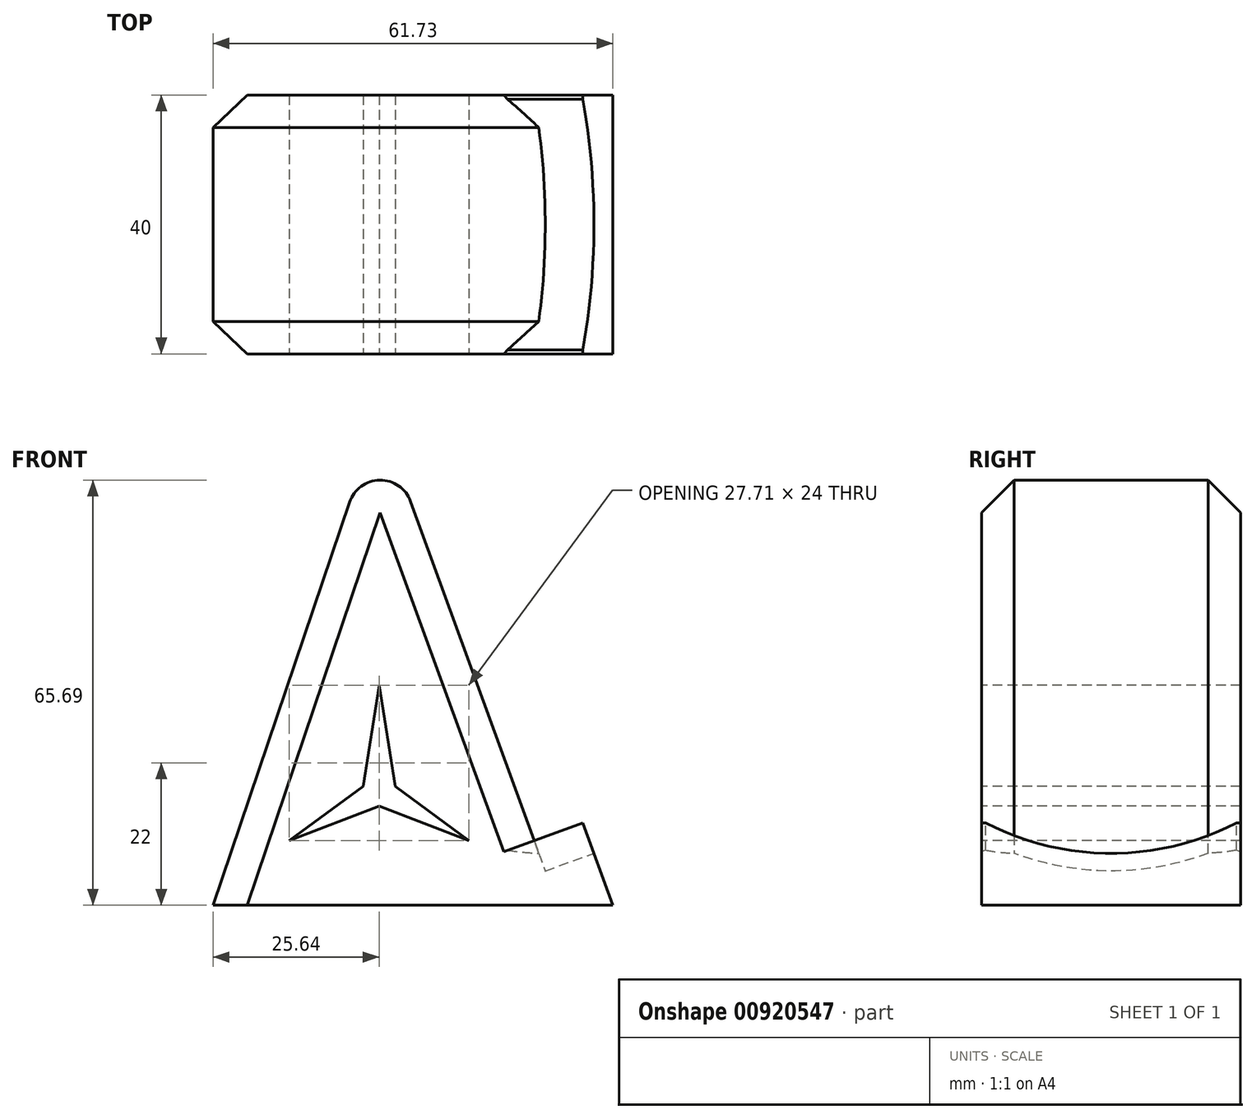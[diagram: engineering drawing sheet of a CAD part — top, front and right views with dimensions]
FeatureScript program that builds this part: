
annotation { "Feature Type Name" : "Feature", "Feature Type Description" : "" }
export const myFeature = defineFeature(function(context is Context, id is Id, definition is map)
    precondition{}
    {
        {
            var Q0;
            Q0=qCreatedBy(makeId("Front.planeOp"),FACE);
            var sketch = newSketch(context, id + "F0", { "sketchPlane" : qUnion([Q0])});
            skLineSegment(sketch, "E0", {"start": v(0, 0) * mm, "end": v(36.1, 0) * mm});
            skLineSegment(sketch, "E1", {"start": v(36.1, 0) * mm, "end": v(31.46, 12.74) * mm});
            skLineSegment(sketch, "E2", {"start": v(31.46, 12.74) * mm, "end": v(23.94, 10) * mm});
            skLineSegment(sketch, "E3", {"start": v(23.94, 10) * mm, "end": v(0, 75.78) * mm});
            skLineSegment(sketch, "E4", {"start": v(0, 75.78) * mm, "end": v(0, 0) * mm, "construction": true});
            skLineSegment(sketch, "E5", {"start": v(0, 75.78) * mm, "end": v(-25.64, 0) * mm});
            skLineSegment(sketch, "E6", {"start": v(-25.64, 0) * mm, "end": v(0, 0) * mm});
            skSolve(sketch);
        }
        {
            var Q0;
            Q0=makeQuery(id+"F0.imprint","IMPRINT",FACE,{"disambiguationData":[TD([[makeQuery(id+"F0.imprint","IMPRINT",EDGE,{"derivedFrom":sQuery(id+"F0.wireOp",EDGE,"E0")}),1.0]])]});
            extrude(context, id + "F1", {"entities" : qUnion([Q0]), "depth" : 40 * mm, "offsetDistance" : 25 * mm});
        }
        {
            var Q0;
            Q0=makeQuery(id+"F1.opExtrude","SWEPT_FACE",FACE,{"disambiguationData":[OSD([sQuery(id+"F0.wireOp",EDGE,"E3")])]});
            var sketch = newSketch(context, id + "F2", { "sketchPlane" : qUnion([Q0])});
            skLineSegment(sketch, "E7", {"start": v(-20, 71.2) * mm, "end": v(-20, 76.2) * mm, "construction": true});
            skLineSegment(sketch, "E8", {"start": v(-20, 71.2) * mm, "end": v(-20, 1.2) * mm, "construction": true});
            skPoint(sketch, "E9", {"position": v(-20, 36.2) * mm});
            skSolve(sketch);
        }
        {
            var Q0;
            Q0=makeQuery(id+"F1.opExtrude","SWEPT_FACE",FACE,{"disambiguationData":[OSD([sQuery(id+"F0.wireOp",EDGE,"E1")])]});
            var sketch = newSketch(context, id + "F3", { "sketchPlane" : qUnion([Q0])});
            skCircle(sketch, "E10", {"center": v(-20, 36.2) * mm, "radius": 40 * mm});
            skSolve(sketch);
        }
        {
            var Q0;
            {var subQ0=sQuery(id+"F3.wireOp",EDGE,"E10");var subQ1=makeQuery(id+"F1.opExtrude","SWEPT_EDGE",EDGE,{"disambiguationData":[OSD([sQuery(id+"F0.wireOp",EDGE,"E1"),sQuery(id+"F0.wireOp",EDGE,"E2")])]});var subQ2=makeQuery(id+"F3.imprint","INTERSECT",VERTEX,{"disambiguationData":[OD(0.0)],"derivedFrom":[subQ1,subQ0]});Q0=makeQuery(id+"F3.imprint","IMPRINT",FACE,{"disambiguationData":[TD([[makeQuery(id+"F3.imprint","IMPRINT",EDGE,{"disambiguationData":[TD([[subQ2,1.0]])],"derivedFrom":subQ0}),1.0]])]});}
            var Q1;
            Q1=makeQuery(id+"F1.opExtrude","SWEPT_FACE",FACE,{"disambiguationData":[OSD([sQuery(id+"F0.wireOp",EDGE,"E3")])]});
            extrude(context, id + "F4", {"entities" : qUnion([Q0]), "operationType" : NewBodyOperationType.REMOVE, "endBound" : BoundingType.UP_TO_SURFACE, "oppositeDirection" : true, "depth" : 25 * mm, "endBoundEntityFace" : qUnion([Q1]), "offsetDistance" : 25 * mm});
        }
        {
            var Q0;
            Q0=makeQuery(id+"F1.opExtrude","SWEPT_EDGE",EDGE,{"disambiguationData":[OSD([sQuery(id+"F0.wireOp",EDGE,"E3"),sQuery(id+"F0.wireOp",EDGE,"E5")])]});
            fillet(context, id + "F5", {"entities" : qUnion([Q0]), "radius" : 5 * mm, "tangentPropagation" : true, "allowEdgeOverflow" : false});
        }
        {
            var Q0;
            Q0=makeQuery(id+"F1.opExtrude","CAP_EDGE",EDGE,{"disambiguationData":[OSD([sQuery(id+"F0.wireOp",EDGE,"E5")])],"isStart":false});
            var Q1;
            Q1=makeQuery(id+"F1.opExtrude","CAP_EDGE",EDGE,{"disambiguationData":[OSD([sQuery(id+"F0.wireOp",EDGE,"E5")])],"isStart":true});
            chamfer(context, id + "F6", {"entities" : qUnion([Q0, Q1]), "width" : 5 * mm, "tangentPropagation" : true});
        }
        {
            var Q0;
            Q0=makeQuery(id+"F1.opExtrude","CAP_FACE",FACE,{"disambiguationData":[OSD([sQuery(id+"F0.wireOp",EDGE,"E0"),sQuery(id+"F0.wireOp",EDGE,"E1"),sQuery(id+"F0.wireOp",EDGE,"E2"),sQuery(id+"F0.wireOp",EDGE,"E3"),sQuery(id+"F0.wireOp",EDGE,"E5"),sQuery(id+"F0.wireOp",EDGE,"E6")])],"isStart":false});
            var sketch = newSketch(context, id + "F7", { "sketchPlane" : qUnion([Q0])});
            skCircle(sketch, "E11.cCircle", {"center": v(0, 18) * mm, "radius": 16 * mm, "construction": true});
            skLineSegment(sketch, "E11.0", {"start": v(0, 34) * mm, "end": v(13.86, 10) * mm, "construction": true});
            skLineSegment(sketch, "E11.1", {"start": v(13.86, 10) * mm, "end": v(-13.86, 10) * mm, "construction": true});
            skLineSegment(sketch, "E11.2", {"start": v(-13.86, 10) * mm, "end": v(0, 34) * mm, "construction": true});
            skLineSegment(sketch, "E12", {"start": v(0, 34) * mm, "end": v(0, 18) * mm, "construction": true});
            skLineSegment(sketch, "E13", {"start": v(0, 18) * mm, "end": v(-13.86, 10) * mm, "construction": true});
            skLineSegment(sketch, "E14", {"start": v(0, 18) * mm, "end": v(13.86, 10) * mm, "construction": true});
            skCircle(sketch, "E15", {"center": v(0, 18) * mm, "radius": 2.5 * mm, "construction": true});
            skLineSegment(sketch, "E16", {"start": v(0, 34) * mm, "end": v(-2.47, 18.4) * mm});
            skLineSegment(sketch, "E17", {"start": v(-2.47, 18.4) * mm, "end": v(-13.86, 10) * mm});
            skLineSegment(sketch, "E18", {"start": v(-13.86, 10) * mm, "end": v(0, 15.32) * mm});
            skLineSegment(sketch, "E19", {"start": v(0, 15.32) * mm, "end": v(13.86, 10) * mm});
            skLineSegment(sketch, "E20", {"start": v(0, 34) * mm, "end": v(2.47, 18.4) * mm});
            skLineSegment(sketch, "E21", {"start": v(2.47, 18.4) * mm, "end": v(13.86, 10) * mm});
            skSolve(sketch);
        }
        {
            var Q0;
            Q0=makeQuery(id+"F7.imprint","IMPRINT",FACE,{"disambiguationData":[TD([[makeQuery(id+"F7.imprint","IMPRINT",EDGE,{"derivedFrom":sQuery(id+"F7.wireOp",EDGE,"E16")}),1.0]])]});
            var Q1;
            Q1=makeQuery(id+"F1.opExtrude","CAP_FACE",FACE,{"disambiguationData":[OSD([sQuery(id+"F0.wireOp",EDGE,"E0"),sQuery(id+"F0.wireOp",EDGE,"E1"),sQuery(id+"F0.wireOp",EDGE,"E2"),sQuery(id+"F0.wireOp",EDGE,"E3"),sQuery(id+"F0.wireOp",EDGE,"E5"),sQuery(id+"F0.wireOp",EDGE,"E6")])],"isStart":true});
            extrude(context, id + "F8", {"entities" : qUnion([Q0]), "operationType" : NewBodyOperationType.REMOVE, "endBound" : BoundingType.UP_TO_SURFACE, "oppositeDirection" : true, "depth" : 25 * mm, "endBoundEntityFace" : qUnion([Q1]), "offsetDistance" : 25 * mm});
        }
    });
